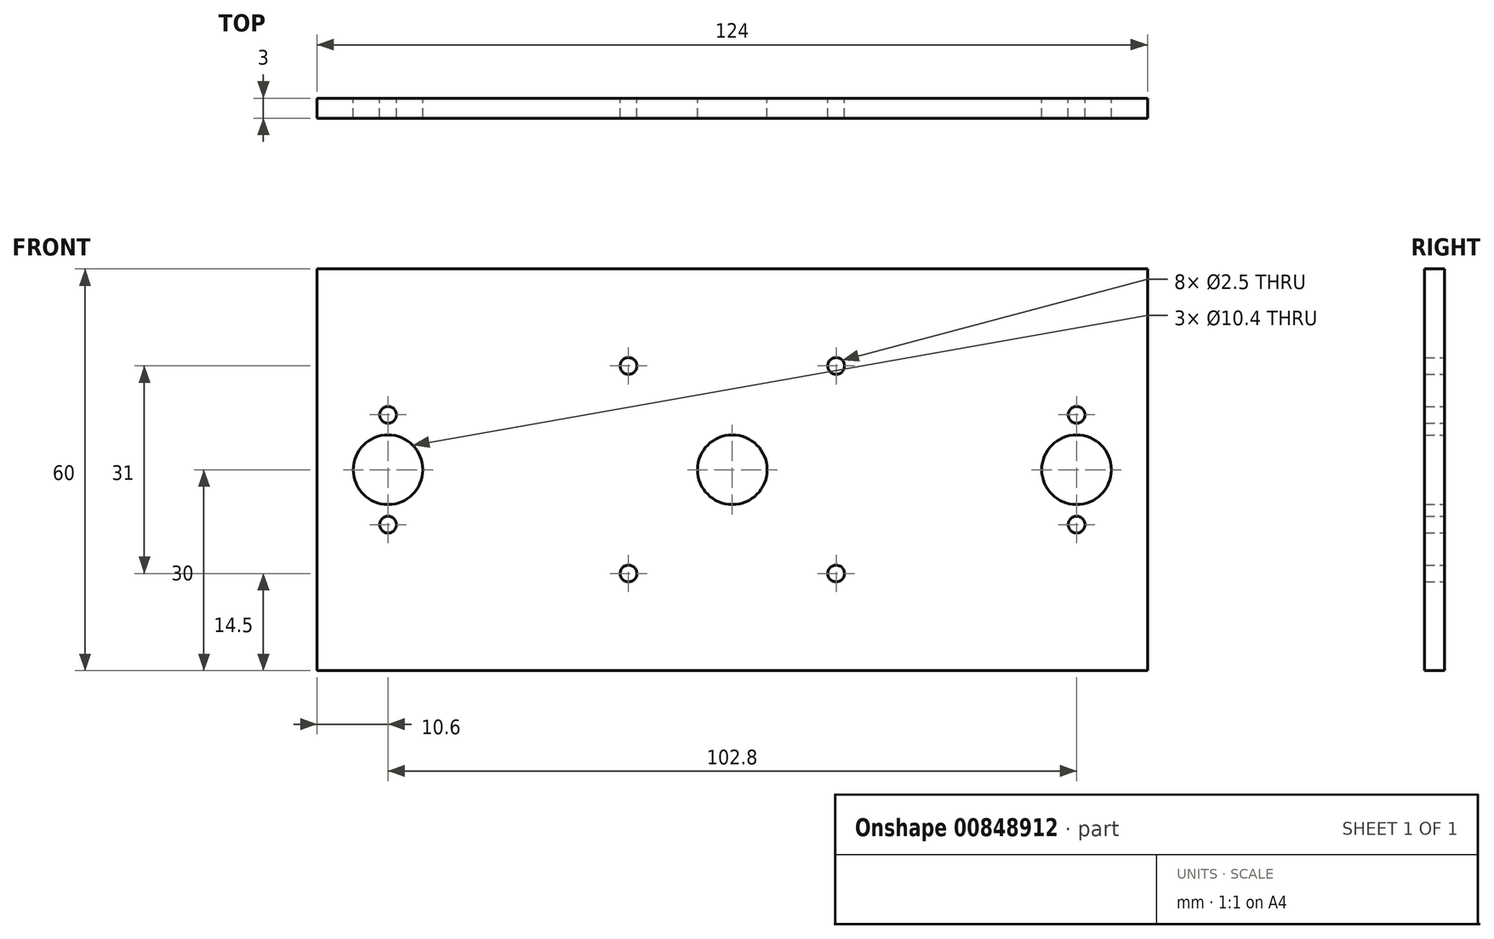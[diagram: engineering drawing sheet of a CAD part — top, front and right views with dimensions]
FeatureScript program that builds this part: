
annotation { "Feature Type Name" : "Feature", "Feature Type Description" : "" }
export const myFeature = defineFeature(function(context is Context, id is Id, definition is map)
    precondition{}
    {
        {
            var Q0;
            Q0=qCreatedBy(makeId("Front.planeOp"),FACE);
            var sketch = newSketch(context, id + "F0", { "sketchPlane" : qUnion([Q0])});
            skPoint(sketch, "E0.middle", {"position": v(0, 0) * mm});
            skCircle(sketch, "E1", {"center": v(0, 0) * mm, "radius": 5.2 * mm});
            skLineSegment(sketch, "E2.bottom", {"start": v(-62, -30) * mm, "end": v(62, -30) * mm});
            skLineSegment(sketch, "E2.top", {"start": v(-62, 30) * mm, "end": v(62, 30) * mm});
            skLineSegment(sketch, "E2.left", {"start": v(-62, -30) * mm, "end": v(-62, 30) * mm});
            skLineSegment(sketch, "E2.right", {"start": v(62, -30) * mm, "end": v(62, 30) * mm});
            skCircle(sketch, "E3", {"center": v(-51.4, 0) * mm, "radius": 5.2 * mm});
            skCircle(sketch, "E4", {"center": v(51.4, 0) * mm, "radius": 5.2 * mm});
            skCircle(sketch, "E5", {"center": v(-51.4, 8.2) * mm, "radius": 1.25 * mm});
            skCircle(sketch, "E6", {"center": v(-51.4, -8.2) * mm, "radius": 1.25 * mm});
            skCircle(sketch, "E7", {"center": v(51.4, 8.2) * mm, "radius": 1.25 * mm});
            skCircle(sketch, "E8", {"center": v(51.4, -8.2) * mm, "radius": 1.25 * mm});
            skCircle(sketch, "E9", {"center": v(-15.5, -15.5) * mm, "radius": 1.25 * mm});
            skCircle(sketch, "E10", {"center": v(15.5, -15.5) * mm, "radius": 1.25 * mm});
            skCircle(sketch, "E11", {"center": v(15.5, 15.5) * mm, "radius": 1.25 * mm});
            skCircle(sketch, "E12", {"center": v(-15.5, 15.5) * mm, "radius": 1.25 * mm});
            skSolve(sketch);
        }
        {
            var Q0;
            Q0=makeQuery(id+"F0.imprint","IMPRINT",FACE,{"disambiguationData":[TD([[makeQuery(id+"F0.imprint","IMPRINT",EDGE,{"derivedFrom":sQuery(id+"F0.wireOp",EDGE,"E1")}),-1.0]])]});
            extrude(context, id + "F1", {"entities" : qUnion([Q0]), "depth" : 3 * mm, "offsetDistance" : 25 * mm});
        }
    });
